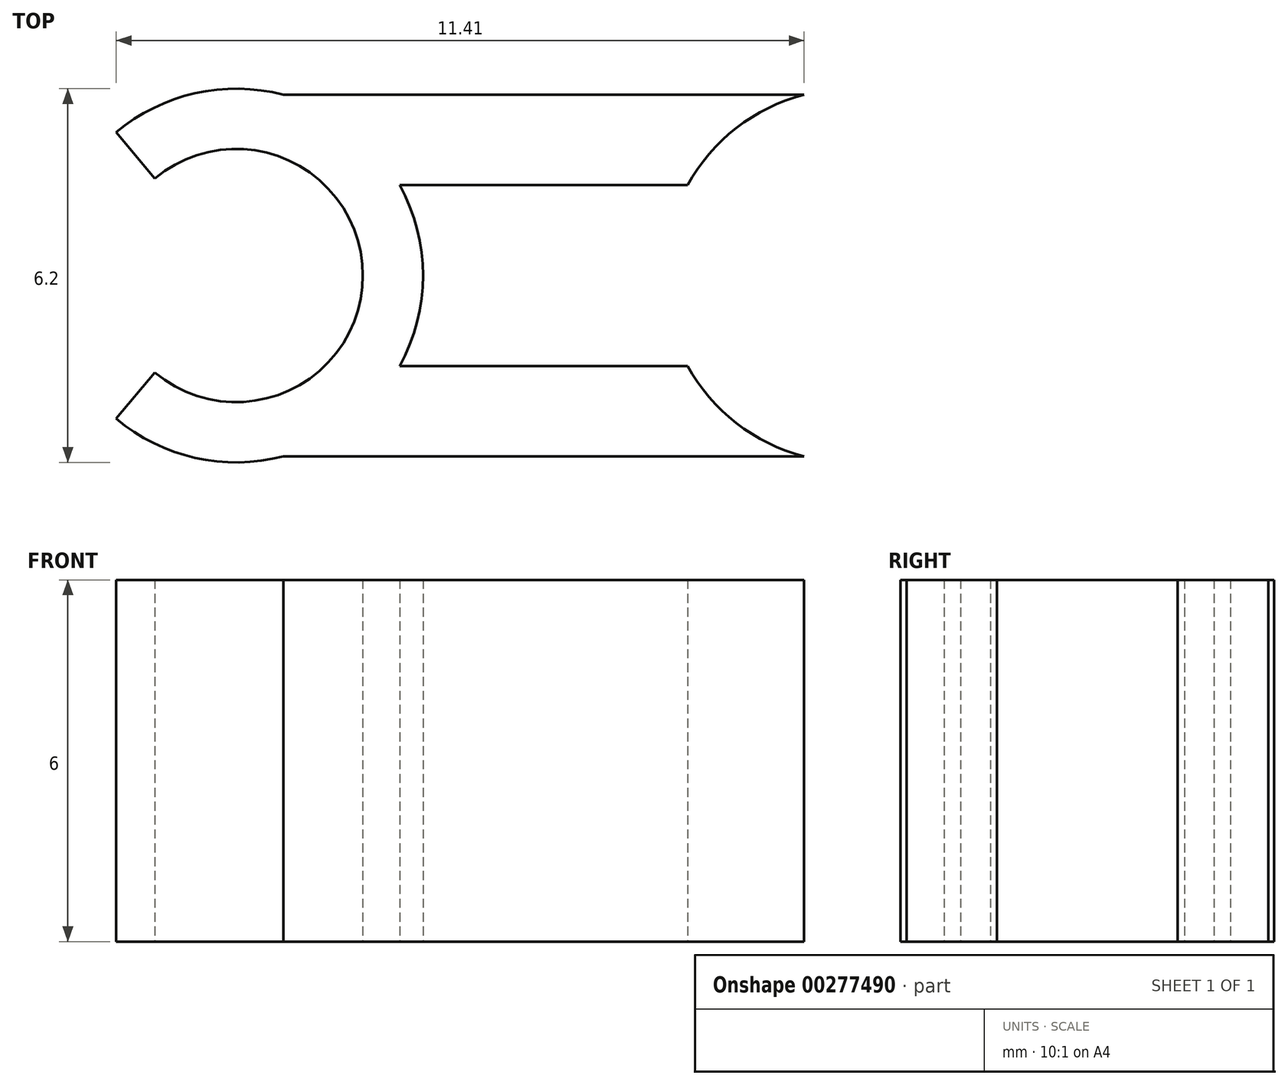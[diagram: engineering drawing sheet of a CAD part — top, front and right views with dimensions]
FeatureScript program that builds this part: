
annotation { "Feature Type Name" : "Feature", "Feature Type Description" : "" }
export const myFeature = defineFeature(function(context is Context, id is Id, definition is map)
    precondition{}
    {
        {
            var Q0;
            Q0=qCreatedBy(makeId("Top.planeOp"),FACE);
            var sketch = newSketch(context, id + "F0", { "sketchPlane" : qUnion([Q0])});
            skPoint(sketch, "E0.middle", {"position": v(0, 0) * mm});
            skArc(sketch, "E1", {"start": v(-6.45, -1.6) * mm, "mid": v(-3, 0) * mm, "end": v(-6.45, 1.6) * mm});
            skArc(sketch, "E2", {"start": v(-7.1, -2.37) * mm, "mid": v(-2, 0) * mm, "end": v(-7.1, 2.37) * mm});
            skLineSegment(sketch, "E3", {"start": v(-5.1, 0) * mm, "end": v(-7.52, 2.89) * mm, "construction": true});
            skLineSegment(sketch, "E4", {"start": v(-5.1, 0) * mm, "end": v(-7.52, -2.89) * mm, "construction": true});
            skLineSegment(sketch, "E5", {"start": v(-7.1, 2.37) * mm, "end": v(-6.45, 1.6) * mm});
            skLineSegment(sketch, "E6", {"start": v(-7.1, -2.37) * mm, "end": v(-6.45, -1.6) * mm});
            skLineSegment(sketch, "E7", {"start": v(0, 7.71) * mm, "end": v(0, -6.45) * mm, "construction": true});
            skArc(sketch, "E8.MirrorCS", {"start": v(7.1, -2.37) * mm, "mid": v(2, 0) * mm, "end": v(7.1, 2.37) * mm});
            skArc(sketch, "E9.MirrorCS", {"start": v(6.45, -1.6) * mm, "mid": v(3, 0) * mm, "end": v(6.45, 1.6) * mm});
            skLineSegment(sketch, "E10.MirrorCS", {"start": v(7.1, -2.37) * mm, "end": v(6.45, -1.6) * mm});
            skLineSegment(sketch, "E11.MirrorCS", {"start": v(7.1, 2.37) * mm, "end": v(6.45, 1.6) * mm});
            skLineSegment(sketch, "E12", {"start": v(-2.39, 1.5) * mm, "end": v(2.39, 1.5) * mm});
            skLineSegment(sketch, "E13", {"start": v(-4.32, 3) * mm, "end": v(4.32, 3) * mm});
            skLineSegment(sketch, "E14", {"start": v(-3.86, 0) * mm, "end": v(4.07, 0) * mm, "construction": true});
            skPoint(sketch, "E14.startSnap0", {"position": v(-2, 0) * mm});
            skPoint(sketch, "E14.endSnap0", {"position": v(3, 0) * mm});
            skLineSegment(sketch, "E15.MirrorCS", {"start": v(-2.39, -1.5) * mm, "end": v(2.39, -1.5) * mm});
            skLineSegment(sketch, "E16.MirrorCS", {"start": v(-4.32, -3) * mm, "end": v(4.32, -3) * mm});
            skSolve(sketch);
        }
        {
            var Q0;
            Q0=makeQuery(id+"F0.imprint","IMPRINT",FACE,{"disambiguationData":[TD([[makeQuery(id+"F0.imprint","IMPRINT",EDGE,{"derivedFrom":sQuery(id+"F0.wireOp",EDGE,"E1")}),-1.0]])]});
            var Q1;
            {var subQ0=sQuery(id+"F0.wireOp",EDGE,"E12");Q1=makeQuery(id+"F0.imprint","IMPRINT",FACE,{"disambiguationData":[TD([[makeQuery(id+"F0.imprint","IMPRINT",EDGE,{"derivedFrom":subQ0}),1.0]])]});}
            var Q2;
            Q2=makeQuery(id+"F0.imprint","IMPRINT",FACE,{"disambiguationData":[TD([[makeQuery(id+"F0.imprint","IMPRINT",EDGE,{"derivedFrom":sQuery(id+"F0.wireOp",EDGE,"E9.MirrorCS")}),1.0]])]});
            var Q3;
            {var subQ0=sQuery(id+"F0.wireOp",EDGE,"E15.MirrorCS");Q3=makeQuery(id+"F0.imprint","IMPRINT",FACE,{"disambiguationData":[TD([[makeQuery(id+"F0.imprint","IMPRINT",EDGE,{"derivedFrom":subQ0}),-1.0]])]});}
            extrude(context, id + "F1", {"entities" : qUnion([Q0, Q1, Q2, Q3]), "depth" : 6 * mm});
        }
    });
